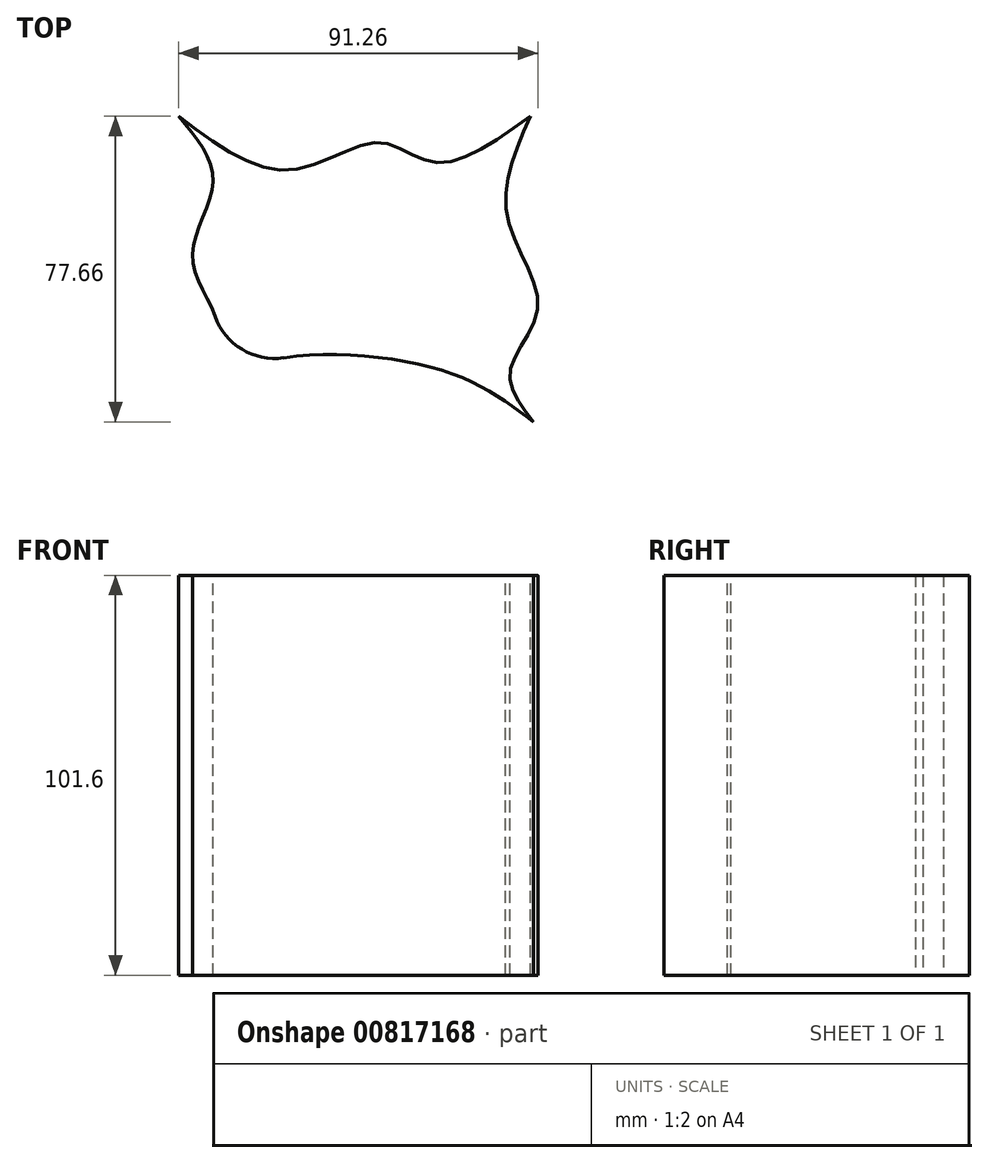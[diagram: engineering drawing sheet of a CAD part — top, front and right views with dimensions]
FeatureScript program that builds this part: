
annotation { "Feature Type Name" : "Feature", "Feature Type Description" : "" }
export const myFeature = defineFeature(function(context is Context, id is Id, definition is map)
    precondition{}
    {
        {
            var Q0;
            Q0=qCreatedBy(makeId("Top.planeOp"),FACE);
            var sketch = newSketch(context, id + "F0", { "sketchPlane" : qUnion([Q0])});
            skLineSegment(sketch, "E0.bottom", {"start": v(-50.8, 38.83) * mm, "end": v(50.8, 38.83) * mm});
            skLineSegment(sketch, "E0.top", {"start": v(-50.8, -38.83) * mm, "end": v(50.8, -38.83) * mm});
            skLineSegment(sketch, "E0.left", {"start": v(-50.8, 38.83) * mm, "end": v(-50.8, -38.83) * mm});
            skLineSegment(sketch, "E0.right", {"start": v(50.8, 38.83) * mm, "end": v(50.8, -38.83) * mm});
            skPoint(sketch, "E0.middle", {"position": v(0, 0) * mm});
            skSolve(sketch);
        }
        {
            var Q0;
            Q0=makeQuery(id+"F0.imprint","IMPRINT",FACE,{"disambiguationData":[TD([[makeQuery(id+"F0.imprint","IMPRINT",EDGE,{"derivedFrom":sQuery(id+"F0.wireOp",EDGE,"E0.bottom")}),-1.0]])]});
            extrude(context, id + "F1", {"entities" : qUnion([Q0]), "depth" : 101.6 * mm, "offsetDistance" : 25.4 * mm});
        }
        {
            var Q0;
            Q0=makeQuery(id+"F1.opExtrude","CAP_FACE",FACE,{"disambiguationData":[OSD([sQuery(id+"F0.wireOp",EDGE,"E0.bottom"),sQuery(id+"F0.wireOp",EDGE,"E0.top"),sQuery(id+"F0.wireOp",EDGE,"E0.left"),sQuery(id+"F0.wireOp",EDGE,"E0.right")])],"isStart":false});
            var sketch = newSketch(context, id + "F2", { "sketchPlane" : qUnion([Q0])});
            skFitSpline(sketch, "E1", {"points": [v(38.54, 38.83) * mm, v(32.7, 13.38) * mm, v(40.43, -9.61) * mm, v(33.46, -25.82) * mm, v(39.3, -38.83) * mm], "startDerivative": vector(-39.75, -90.24) * mm, "endDerivative": vector(46.87, -60.97) * mm});
            skSolve(sketch);
        }
        {
            var Q0;
            {var subQ0=sQuery(id+"F2.wireOp",EDGE,"E1");Q0=makeQuery(id+"F2.imprint","IMPRINT",FACE,{"disambiguationData":[TD([[makeQuery(id+"F2.imprint","IMPRINT",EDGE,{"derivedFrom":subQ0}),1.0]])]});}
            extrude(context, id + "F3", {"entities" : qUnion([Q0]), "operationType" : NewBodyOperationType.REMOVE, "oppositeDirection" : true, "depth" : 101.6 * mm, "offsetDistance" : 25.4 * mm});
        }
        {
            var Q0;
            Q0=makeQuery(id+"F1.opExtrude","CAP_FACE",FACE,{"disambiguationData":[OSD([sQuery(id+"F0.wireOp",EDGE,"E0.bottom"),sQuery(id+"F0.wireOp",EDGE,"E0.top"),sQuery(id+"F0.wireOp",EDGE,"E0.left"),sQuery(id+"F0.wireOp",EDGE,"E0.right")])],"isStart":false});
            var sketch = newSketch(context, id + "F4", { "sketchPlane" : qUnion([Q0])});
            skFitSpline(sketch, "E2", {"points": [v(38.54, 38.83) * mm, v(14.51, 27.05) * mm, v(0, 32.14) * mm, v(-22.43, 25.16) * mm, v(-50.8, 38.83) * mm], "startDerivative": vector(-97.52, -70.57) * mm, "endDerivative": vector(-99.4, 75.13) * mm});
            skSolve(sketch);
        }
        {
            var Q0;
            Q0=makeQuery(id+"F4.imprint","IMPRINT",FACE,{"disambiguationData":[TD([[makeQuery(id+"F4.imprint","IMPRINT",EDGE,{"derivedFrom":sQuery(id+"F4.wireOp",EDGE,"E2")}),-1.0]])]});
            extrude(context, id + "F5", {"entities" : qUnion([Q0]), "operationType" : NewBodyOperationType.REMOVE, "oppositeDirection" : true, "depth" : 101.6 * mm, "offsetDistance" : 25.4 * mm});
        }
        {
            var Q0;
            Q0=makeQuery(id+"F1.opExtrude","CAP_FACE",FACE,{"disambiguationData":[OSD([sQuery(id+"F0.wireOp",EDGE,"E0.bottom"),sQuery(id+"F0.wireOp",EDGE,"E0.top"),sQuery(id+"F0.wireOp",EDGE,"E0.left"),sQuery(id+"F0.wireOp",EDGE,"E0.right")])],"isStart":false});
            var sketch = newSketch(context, id + "F6", { "sketchPlane" : qUnion([Q0])});
            skFitSpline(sketch, "E3", {"points": [v(-50.8, 38.83) * mm, v(-42.03, 22.15) * mm, v(-47.3, 3.1) * mm, v(-40.71, -15.55) * mm, v(-50.8, -38.83) * mm], "startDerivative": vector(56.88, -67.84) * mm, "endDerivative": vector(-59.42, -86.93) * mm});
            skSolve(sketch);
        }
        {
            var Q0;
            Q0=makeQuery(id+"F6.imprint","IMPRINT",FACE,{"disambiguationData":[TD([[makeQuery(id+"F6.imprint","IMPRINT",EDGE,{"derivedFrom":sQuery(id+"F6.wireOp",EDGE,"E3")}),-1.0]])]});
            extrude(context, id + "F7", {"entities" : qUnion([Q0]), "operationType" : NewBodyOperationType.REMOVE, "oppositeDirection" : true, "depth" : 101.6 * mm, "offsetDistance" : 25.4 * mm});
        }
        {
            var Q0;
            Q0=makeQuery(id+"F1.opExtrude","CAP_FACE",FACE,{"disambiguationData":[OSD([sQuery(id+"F0.wireOp",EDGE,"E0.bottom"),sQuery(id+"F0.wireOp",EDGE,"E0.top"),sQuery(id+"F0.wireOp",EDGE,"E0.left"),sQuery(id+"F0.wireOp",EDGE,"E0.right")])],"isStart":false});
            var sketch = newSketch(context, id + "F8", { "sketchPlane" : qUnion([Q0])});
            skFitSpline(sketch, "E4", {"points": [v(39.3, -38.83) * mm, v(15.46, -25.54) * mm, v(-32.98, -24.6) * mm, v(-50.8, -38.83) * mm], "startDerivative": vector(-64.08, 49.03) * mm, "endDerivative": vector(-48.52, -59.7) * mm});
            skSolve(sketch);
        }
        {
            var Q0;
            Q0=makeQuery(id+"F8.imprint","IMPRINT",FACE,{"disambiguationData":[TD([[makeQuery(id+"F8.imprint","IMPRINT",EDGE,{"derivedFrom":sQuery(id+"F8.wireOp",EDGE,"E4")}),1.0]])]});
            extrude(context, id + "F9", {"entities" : qUnion([Q0]), "operationType" : NewBodyOperationType.REMOVE, "oppositeDirection" : true, "depth" : 101.6 * mm, "offsetDistance" : 25.4 * mm});
        }
        {
            var Q0;
            {var subQ0=sQuery(id+"F6.wireOp",EDGE,"E3");var subQ1=sQuery(id+"F0.wireOp",EDGE,"E0.top");var subQ2=sQuery(id+"F0.wireOp",EDGE,"E0.left");Q0=makeQuery(id+"F9.boolean.opBoolean","MERGE",EDGE,{"derivedFrom":[makeQuery(id+"F7.boolean.opBoolean","MERGE",EDGE,{"derivedFrom":[makeQuery(id+"F1.opExtrude","SWEPT_EDGE",EDGE,{"disambiguationData":[OSD([subQ1,subQ2])]}),makeQuery(id+"F7.opExtrude","SWEPT_EDGE",EDGE,{"disambiguationData":[OSD([subQ1,subQ2,subQ0])]})]}),makeQuery(id+"F9.opExtrude","SWEPT_EDGE",EDGE,{"disambiguationData":[OSD([subQ1,subQ0,sQuery(id+"F8.wireOp",EDGE,"E4")])]})]});}
            var Q1;
            {var subQ0=sQuery(id+"F2.wireOp",EDGE,"E1");var subQ1=sQuery(id+"F0.wireOp",EDGE,"E0.top");Q1=makeQuery(id+"F9.boolean.opBoolean","MERGE",EDGE,{"derivedFrom":[makeQuery(id+"F3.boolean.opBoolean","COPY",EDGE,{"derivedFrom":makeQuery(id+"F3.opExtrude","SWEPT_EDGE",EDGE,{"disambiguationData":[OSD([subQ1,subQ0])]})}),makeQuery(id+"F9.opExtrude","SWEPT_EDGE",EDGE,{"disambiguationData":[OSD([subQ1,subQ0,sQuery(id+"F8.wireOp",EDGE,"E4")])]})]});}
            var Q2;
            {var subQ0=sQuery(id+"F2.wireOp",EDGE,"E1");var subQ1=sQuery(id+"F0.wireOp",EDGE,"E0.bottom");Q2=makeQuery(id+"F5.boolean.opBoolean","MERGE",EDGE,{"derivedFrom":[makeQuery(id+"F3.boolean.opBoolean","COPY",EDGE,{"derivedFrom":makeQuery(id+"F3.opExtrude","SWEPT_EDGE",EDGE,{"disambiguationData":[OSD([subQ1,subQ0])]})}),makeQuery(id+"F5.opExtrude","SWEPT_EDGE",EDGE,{"disambiguationData":[OSD([subQ1,subQ0,sQuery(id+"F4.wireOp",EDGE,"E2")])]})]});}
            fillet(context, id + "F10", {"entities" : qUnion([Q0, Q1, Q2]), "radius" : 16.09 * mm, "tangentPropagation" : true, "allowEdgeOverflow" : false});
        }
    });
